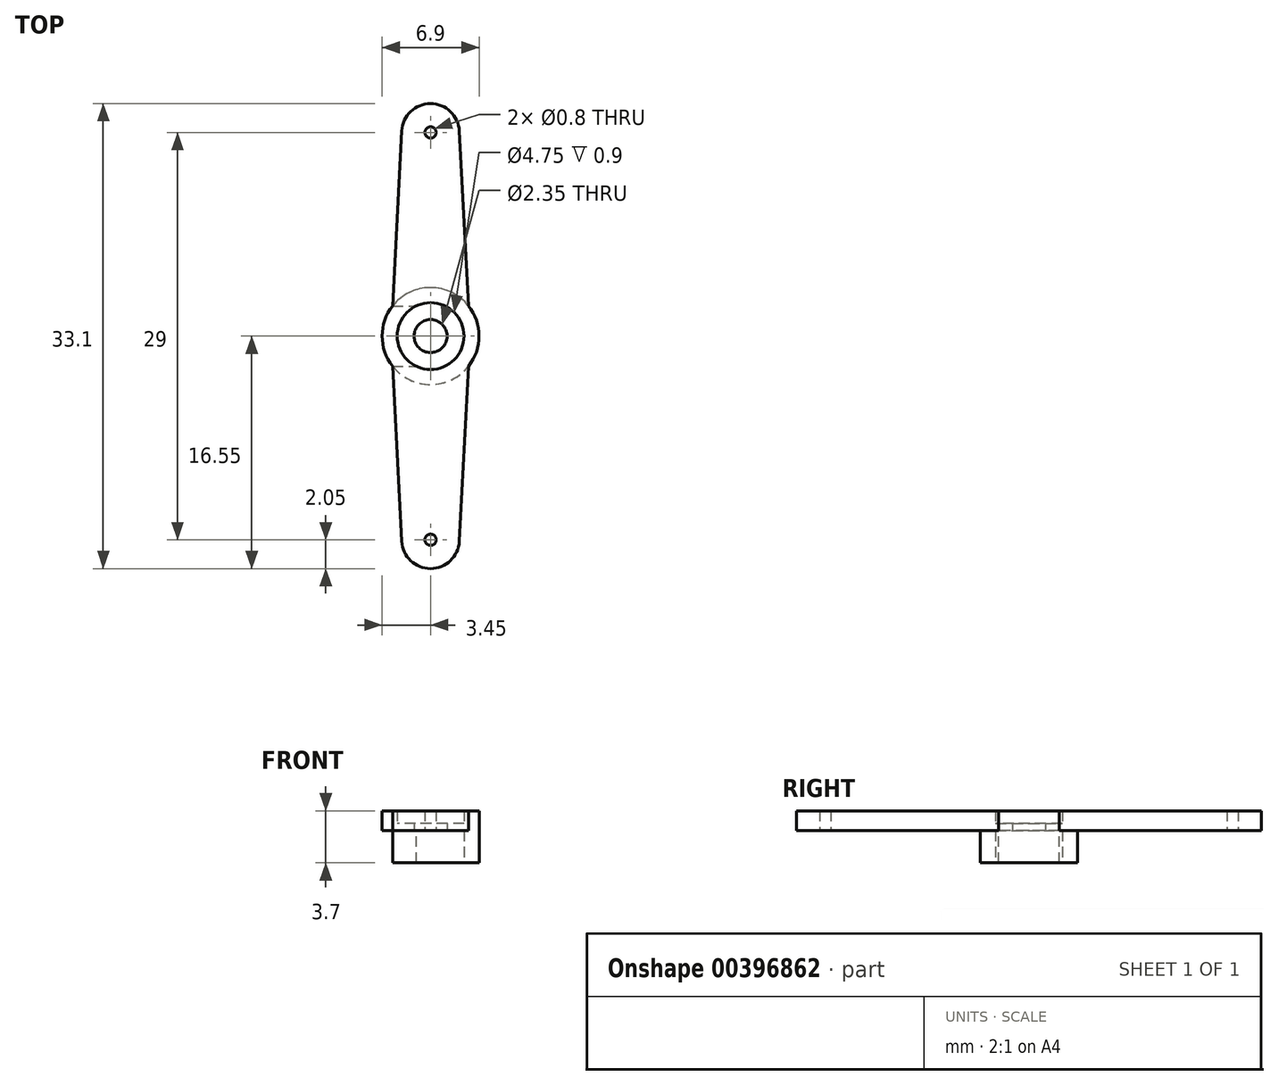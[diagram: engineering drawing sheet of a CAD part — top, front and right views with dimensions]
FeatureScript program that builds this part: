
annotation { "Feature Type Name" : "Feature", "Feature Type Description" : "" }
export const myFeature = defineFeature(function(context is Context, id is Id, definition is map)
    precondition{}
    {
        {
            var Q0;
            Q0=qCreatedBy(makeId("Top.planeOp"),FACE);
            var sketch = newSketch(context, id + "F0", { "sketchPlane" : qUnion([Q0])});
            skCircle(sketch, "E0", {"center": v(0, 0) * mm, "radius": 3.45 * mm});
            skCircle(sketch, "E1", {"center": v(0, 0) * mm, "radius": 2.38 * mm});
            skCircle(sketch, "E2", {"center": v(0, 0) * mm, "radius": 1.18 * mm});
            skCircle(sketch, "E3", {"center": v(0, 14.5) * mm, "radius": 0.4 * mm});
            skCircle(sketch, "E4", {"center": v(0, 14.5) * mm, "radius": 2.05 * mm});
            skLineSegment(sketch, "E5", {"start": v(-2.7, 2.15) * mm, "end": v(-2.05, 14.6) * mm});
            skLineSegment(sketch, "E6", {"start": v(2.05, 14.6) * mm, "end": v(2.7, 2.15) * mm});
            skLineSegment(sketch, "E7", {"start": v(-2.7, 2.15) * mm, "end": v(2.7, 2.15) * mm});
            skLineSegment(sketch, "E8", {"start": v(0, 2.15) * mm, "end": v(0, 0) * mm});
            skCircle(sketch, "E9", {"center": v(0, -14.5) * mm, "radius": 0.4 * mm});
            skCircle(sketch, "E10", {"center": v(0, -14.5) * mm, "radius": 2.05 * mm});
            skLineSegment(sketch, "E11", {"start": v(-2.7, -2.15) * mm, "end": v(-2.05, -14.6) * mm});
            skLineSegment(sketch, "E12", {"start": v(2.05, -14.6) * mm, "end": v(2.7, -2.15) * mm});
            skLineSegment(sketch, "E13", {"start": v(-2.7, -2.15) * mm, "end": v(2.7, -2.15) * mm});
            skSolve(sketch);
        }
        {
            var Q0;
            Q0=qSketchRegion(id+"F0",true);
            extrude(context, id + "F1", {"entities" : qUnion([Q0]), "depth" : 1.4 * mm});
        }
        {
            var Q0;
            {var subQ0=sQuery(id+"F0.wireOp",EDGE,"E7");var subQ4=sQuery(id+"F0.wireOp",EDGE,"E1");var subQ5=makeQuery(id+"F0.imprint","INTERSECT",VERTEX,{"disambiguationData":[OD(0.0)],"derivedFrom":[subQ4,subQ0]});Q0=makeQuery(id+"F0.imprint","IMPRINT",FACE,{"disambiguationData":[TD([[makeQuery(id+"F0.imprint","IMPRINT",EDGE,{"disambiguationData":[TD([[subQ5,-1.0]])],"derivedFrom":subQ4}),-1.0]])]});}
            var Q1;
            {var subQ0=sQuery(id+"F0.wireOp",EDGE,"E7");var subQ4=sQuery(id+"F0.wireOp",EDGE,"E1");var subQ5=makeQuery(id+"F0.imprint","INTERSECT",VERTEX,{"disambiguationData":[OD(0.0)],"derivedFrom":[subQ4,subQ0]});Q1=makeQuery(id+"F0.imprint","IMPRINT",FACE,{"disambiguationData":[TD([[makeQuery(id+"F0.imprint","IMPRINT",EDGE,{"disambiguationData":[TD([[subQ5,1.0]])],"derivedFrom":subQ4}),-1.0]])]});}
            var Q2;
            {var subQ0=sQuery(id+"F0.wireOp",EDGE,"E13");var subQ4=sQuery(id+"F0.wireOp",EDGE,"E1");var subQ5=makeQuery(id+"F0.imprint","INTERSECT",VERTEX,{"disambiguationData":[OD(0.0)],"derivedFrom":[subQ4,subQ0]});Q2=makeQuery(id+"F0.imprint","IMPRINT",FACE,{"disambiguationData":[TD([[makeQuery(id+"F0.imprint","IMPRINT",EDGE,{"disambiguationData":[TD([[subQ5,-1.0]])],"derivedFrom":subQ4}),-1.0]])]});}
            var Q3;
            {var subQ0=sQuery(id+"F0.wireOp",EDGE,"E7");var subQ5=sQuery(id+"F0.wireOp",EDGE,"E1");var subQ6=makeQuery(id+"F0.imprint","INTERSECT",VERTEX,{"disambiguationData":[OD(1.0)],"derivedFrom":[subQ5,subQ0]});Q3=makeQuery(id+"F0.imprint","IMPRINT",FACE,{"disambiguationData":[TD([[makeQuery(id+"F0.imprint","IMPRINT",EDGE,{"disambiguationData":[TD([[subQ6,1.0]])],"derivedFrom":subQ5}),-1.0]])]});}
            extrude(context, id + "F2", {"entities" : qUnion([Q0, Q1, Q2, Q3]), "operationType" : NewBodyOperationType.ADD, "oppositeDirection" : true, "depth" : 2.3 * mm});
        }
        {
            var Q0;
            Q0=makeQuery(id+"F0.imprint","IMPRINT",FACE,{"disambiguationData":[TD([[makeQuery(id+"F0.imprint","IMPRINT",EDGE,{"derivedFrom":sQuery(id+"F0.wireOp",EDGE,"E2")}),-1.0]])]});
            var Q1;
            {var subQ0=sQuery(id+"F0.wireOp",EDGE,"E7");var subQ4=makeQuery(id+"F0.imprint","IMPRINT",VERTEX,{"derivedFrom":subQ0});Q1=makeQuery(id+"F0.imprint","IMPRINT",FACE,{"disambiguationData":[TD([[makeQuery(id+"F0.imprint","IMPRINT",EDGE,{"disambiguationData":[TD([[subQ4,1.0]])],"derivedFrom":subQ0}),1.0]])]});}
            var Q2;
            {var subQ0=sQuery(id+"F0.wireOp",EDGE,"E13");var subQ1=sQuery(id+"F0.wireOp",EDGE,"E1");var subQ2=makeQuery(id+"F0.imprint","INTERSECT",VERTEX,{"disambiguationData":[OD(0.0)],"derivedFrom":[subQ1,subQ0]});Q2=makeQuery(id+"F0.imprint","IMPRINT",FACE,{"disambiguationData":[TD([[makeQuery(id+"F0.imprint","IMPRINT",EDGE,{"disambiguationData":[TD([[subQ2,-1.0]])],"derivedFrom":subQ1}),1.0]])]});}
            extrude(context, id + "F3", {"entities" : qUnion([Q0, Q1, Q2]), "operationType" : NewBodyOperationType.ADD, "depth" : .5 * mm});
        }
    });
